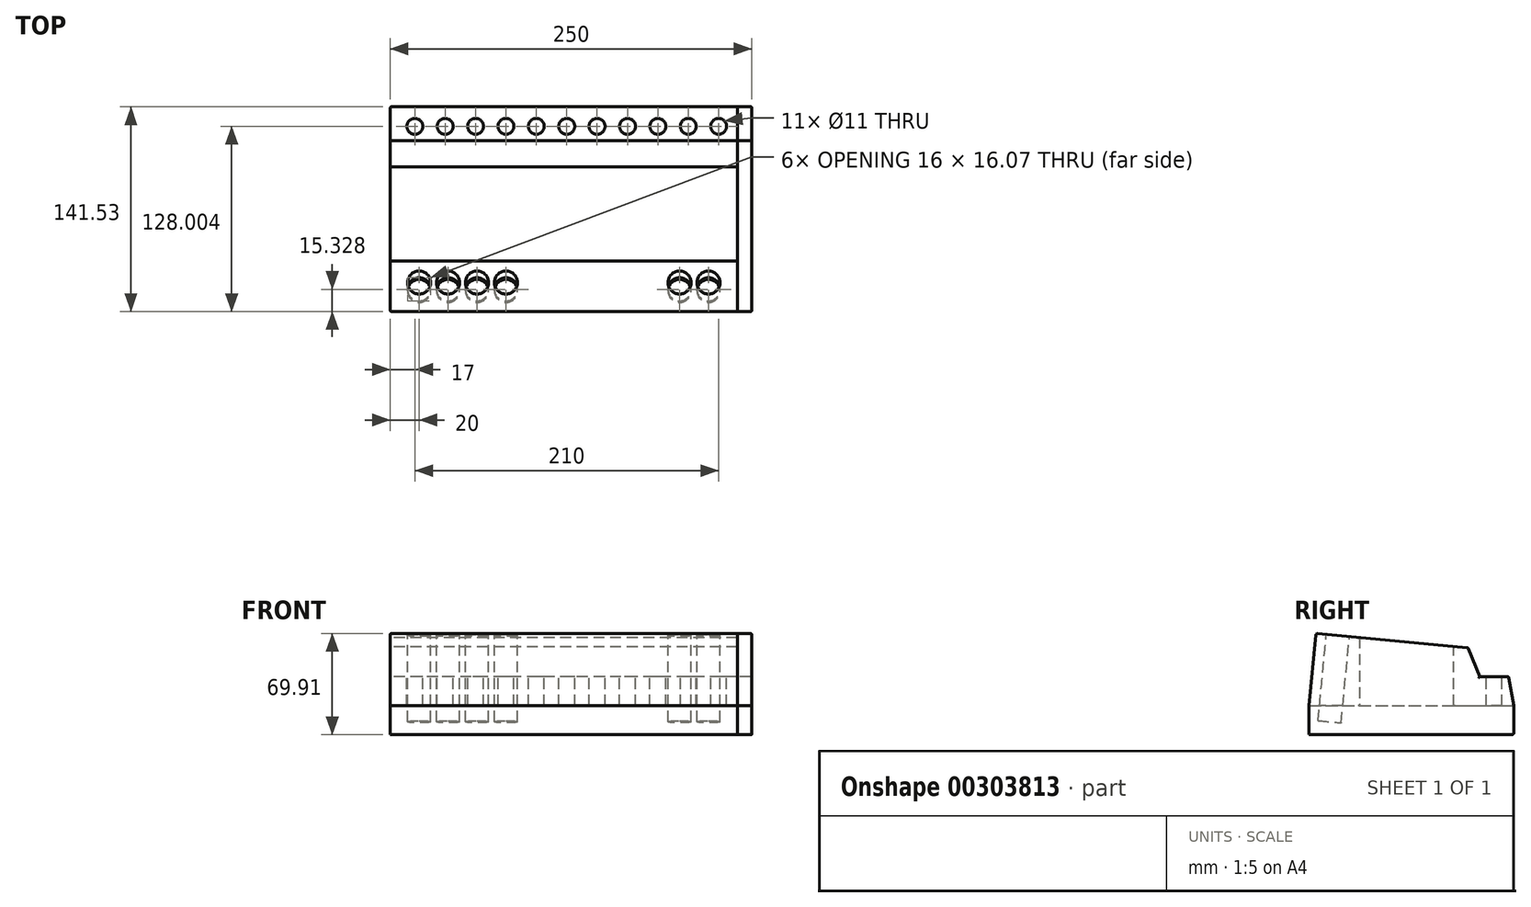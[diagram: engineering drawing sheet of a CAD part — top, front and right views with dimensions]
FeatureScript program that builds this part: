
annotation { "Feature Type Name" : "Feature", "Feature Type Description" : "" }
export const myFeature = defineFeature(function(context is Context, id is Id, definition is map)
    precondition{}
    {
        {
            var Q0;
            Q0=qCreatedBy(makeId("Right.planeOp"),FACE);
            var sketch = newSketch(context, id + "F0", { "sketchPlane" : qUnion([Q0])});
            skLineSegment(sketch, "E0", {"start": v(-106.53, 67.11) * mm, "end": v(-106.53, 20) * mm});
            skLineSegment(sketch, "E1", {"start": v(-41.53, 20) * mm, "end": v(-41.53, 60.85) * mm});
            skLineSegment(sketch, "E2", {"start": v(-41.53, 60.85) * mm, "end": v(-31.57, 59.9) * mm});
            skLineSegment(sketch, "E3", {"start": v(-31.57, 59.9) * mm, "end": v(-23.53, 40) * mm});
            skLineSegment(sketch, "E4", {"start": v(-23.53, 40) * mm, "end": v(-3.53, 40) * mm});
            skLineSegment(sketch, "E5", {"start": v(-3.53, 40) * mm, "end": v(0, 20) * mm});
            skLineSegment(sketch, "E6", {"start": v(-141.53, 20) * mm, "end": v(-136.53, 70) * mm});
            skLineSegment(sketch, "E7", {"start": v(-175.18, 73.72) * mm, "end": v(36.57, 53.33) * mm, "construction": true});
            skLineSegment(sketch, "E8", {"start": v(-136.53, 70) * mm, "end": v(-106.53, 67.11) * mm});
            skLineSegment(sketch, "E9", {"start": v(-141.53, 20) * mm, "end": v(-106.53, 20) * mm});
            skLineSegment(sketch, "E10", {"start": v(-176.43, 20) * mm, "end": v(39.02, 20) * mm, "construction": true});
            skLineSegment(sketch, "E11", {"start": v(-41.53, 20) * mm, "end": v(0, 20) * mm});
            skSolve(sketch);
        }
        {
            var Q0;
            Q0 = qSketchRegion(id + "F0", true);
            extrude(context, id + "F1", {"entities" : qUnion([Q0]), "endBound" : BoundingType.SYMMETRIC, "depth" : 240 * mm});
        }
        {
            var Q0;
            Q0=qCreatedBy(makeId("Right.planeOp"),FACE);
            var sketch = newSketch(context, id + "F2", { "sketchPlane" : qUnion([Q0])});
            skLineSegment(sketch, "E12.bottom", {"start": v(-141.53, 20) * mm, "end": v(0, 20) * mm});
            skLineSegment(sketch, "E12.top", {"start": v(-141.53, 0) * mm, "end": v(0, 0) * mm});
            skLineSegment(sketch, "E12.left", {"start": v(-141.53, 20) * mm, "end": v(-141.53, 0) * mm});
            skLineSegment(sketch, "E12.right", {"start": v(0, 20) * mm, "end": v(0, 0) * mm});
            skSolve(sketch);
        }
        {
            var Q0;
            Q0 = qSketchRegion(id + "F2", true);
            extrude(context, id + "F3", {"entities" : qUnion([Q0]), "endBound" : BoundingType.SYMMETRIC, "depth" : 240 * mm});
        }
        {
            var Q0;
            Q0=makeQuery(id+"F1.opExtrude","SWEPT_FACE",FACE,{"disambiguationData":[OSD([sQuery(id+"F0.wireOp",EDGE,"E8")])]});
            var sketch = newSketch(context, id + "F4", { "sketchPlane" : qUnion([Q0])});
            skLineSegment(sketch, "E13", {"start": v(120, -127.54) * mm, "end": v(-120, -127.54) * mm, "construction": true});
            skCircle(sketch, "E14", {"center": v(-100, -127.54) * mm, "radius": 8 * mm});
            skCircle(sketch, "E15", {"center": v(100, -127.54) * mm, "radius": 8 * mm});
            skCircle(sketch, "E16", {"center": v(80, -127.54) * mm, "radius": 8 * mm});
            skCircle(sketch, "E17.1.0.0", {"center": v(-80, -127.54) * mm, "radius": 8 * mm});
            skCircle(sketch, "E17.2.0.0", {"center": v(-60, -127.54) * mm, "radius": 8 * mm});
            skCircle(sketch, "E17.3.0.0", {"center": v(-40, -127.54) * mm, "radius": 8 * mm});
            skLineSegment(sketch, "E17.direction1", {"start": v(-100, -127.54) * mm, "end": v(-80, -127.54) * mm, "construction": true});
            skSolve(sketch);
        }
        {
            var Q0;
            Q0 = qSketchRegion(id + "F4", true);
            extrude(context, id + "F5", {"entities" : qUnion([Q0]), "operationType" : NewBodyOperationType.REMOVE, "oppositeDirection" : true, "depth" : 60 * mm});
        }
        {
            var Q0;
            Q0=makeQuery(id+"F1.opExtrude","SWEPT_FACE",FACE,{"disambiguationData":[OSD([sQuery(id+"F0.wireOp",EDGE,"E4")])]});
            var sketch = newSketch(context, id + "F6", { "sketchPlane" : qUnion([Q0])});
            skCircle(sketch, "E18", {"center": v(107, -13.53) * mm, "radius": 5.5 * mm});
            skCircle(sketch, "E19.1.0.0", {"center": v(86, -13.53) * mm, "radius": 5.5 * mm});
            skCircle(sketch, "E19.2.0.0", {"center": v(65, -13.53) * mm, "radius": 5.5 * mm});
            skCircle(sketch, "E19.3.0.0", {"center": v(44, -13.53) * mm, "radius": 5.5 * mm});
            skCircle(sketch, "E19.4.0.0", {"center": v(23, -13.53) * mm, "radius": 5.5 * mm});
            skLineSegment(sketch, "E19.direction1", {"start": v(107, -13.53) * mm, "end": v(86, -13.53) * mm, "construction": true});
            skLineSegment(sketch, "E19.direction2", {"start": v(107, -13.53) * mm, "end": v(107, 6.47) * mm, "construction": true});
            skCircle(sketch, "E20.0.5.0", {"center": v(2, -13.53) * mm, "radius": 5.5 * mm});
            skCircle(sketch, "E20.0.6.0", {"center": v(-19, -13.53) * mm, "radius": 5.5 * mm});
            skCircle(sketch, "E20.0.7.0", {"center": v(-40, -13.53) * mm, "radius": 5.5 * mm});
            skCircle(sketch, "E20.0.8.0", {"center": v(-61, -13.53) * mm, "radius": 5.5 * mm});
            skCircle(sketch, "E20.0.9.0", {"center": v(-82, -13.53) * mm, "radius": 5.5 * mm});
            skCircle(sketch, "E21.0.10.0", {"center": v(-103, -13.53) * mm, "radius": 5.5 * mm});
            skSolve(sketch);
        }
        {
            var Q0;
            Q0 = qSketchRegion(id + "F6", true);
            extrude(context, id + "F7", {"entities" : qUnion([Q0]), "operationType" : NewBodyOperationType.REMOVE, "oppositeDirection" : true, "depth" : 20 * mm});
        }
        {
            var Q0;
            Q0=makeQuery(id+"F1.opExtrude","CAP_FACE",FACE,{"disambiguationData":[OSD([sQuery(id+"F0.wireOp",EDGE,"tw387ZvV-JYj8-68VL-s3yb-Uck8thZa5wHs"),sQuery(id+"F0.wireOp",EDGE,"NKL3wcGp-Pg8C-4RBL-oGj4-fkOtX3Kfw7oe"),sQuery(id+"F0.wireOp",EDGE,"E0"),sQuery(id+"F0.wireOp",EDGE,"q42HuZwT-Lavk-Tpkk-W9Jl-RTIdizZQmuwW"),sQuery(id+"F0.wireOp",EDGE,"E1"),sQuery(id+"F0.wireOp",EDGE,"E2"),sQuery(id+"F0.wireOp",EDGE,"E3"),sQuery(id+"F0.wireOp",EDGE,"E4"),sQuery(id+"F0.wireOp",EDGE,"E5"),sQuery(id+"F0.wireOp",EDGE,"b2ctV8Q4-d0uH-XkVO-mPFh-DvxioqJfeffP"),sQuery(id+"F0.wireOp",EDGE,"nbkesUFM-ipBm-tUCA-T4BL-iNUQwh1iUt4A"),sQuery(id+"F0.wireOp",EDGE,"E6")])],"isStart":false});
            var sketch = newSketch(context, id + "F8", { "sketchPlane" : qUnion([Q0])});
            skLineSegment(sketch, "E22", {"start": v(-141.53, 20) * mm, "end": v(-141.53, 20) * mm});
            skLineSegment(sketch, "E23", {"start": v(-141.53, 20) * mm, "end": v(-141.53, 0) * mm});
            skLineSegment(sketch, "E24", {"start": v(-141.53, 0) * mm, "end": v(0, 0) * mm});
            skLineSegment(sketch, "E25", {"start": v(-3.53, 40) * mm, "end": v(-3.53, 40) * mm});
            skLineSegment(sketch, "E26", {"start": v(-3.53, 40) * mm, "end": v(-23.53, 40) * mm});
            skLineSegment(sketch, "E27", {"start": v(-23.53, 40) * mm, "end": v(-31.57, 59.9) * mm});
            skLineSegment(sketch, "E28", {"start": v(-31.57, 59.9) * mm, "end": v(-136.53, 70) * mm});
            skLineSegment(sketch, "E29", {"start": v(-136.53, 70) * mm, "end": v(-141.53, 20) * mm});
            skLineSegment(sketch, "E30", {"start": v(-3.53, 40) * mm, "end": v(0, 20) * mm});
            skLineSegment(sketch, "E31", {"start": v(0, 20) * mm, "end": v(0, 0) * mm});
            skSolve(sketch);
        }
        {
            var Q0;
            Q0 = qSketchRegion(id + "F8", true);
            extrude(context, id + "F9", {"entities" : qUnion([Q0]), "depth" : 10 * mm});
        }
        {
            var Q0;
            Q0=makeQuery(id+"F1.opExtrude","SWEPT_EDGE",EDGE,{"disambiguationData":[OSD([sQuery(id+"F0.wireOp",EDGE,"E4"),sQuery(id+"F0.wireOp",EDGE,"E5")])]});
            var Q1;
            Q1=makeQuery(id+"F1.opExtrude","SWEPT_EDGE",EDGE,{"disambiguationData":[OSD([sQuery(id+"F0.wireOp",EDGE,"E2"),sQuery(id+"F0.wireOp",EDGE,"E3")])]});
            var Q2;
            Q2=makeQuery(id+"F1.opExtrude","SWEPT_EDGE",EDGE,{"disambiguationData":[OSD([sQuery(id+"F0.wireOp",EDGE,"E1"),sQuery(id+"F0.wireOp",EDGE,"E2")])]});
            var Q3;
            Q3=makeQuery(id+"F3.opExtrude","SWEPT_EDGE",EDGE,{"disambiguationData":[OSD([sQuery(id+"F2.wireOp",EDGE,"E12.top"),sQuery(id+"F2.wireOp",EDGE,"E12.right")])]});
            var Q4;
            Q4=makeQuery(id+"F9.opExtrude","SWEPT_EDGE",EDGE,{"disambiguationData":[OSD([sQuery(id+"F8.wireOp",EDGE,"E24"),sQuery(id+"F8.wireOp",EDGE,"E31")])]});
            var Q5;
            Q5=makeQuery(id+"F9.opExtrude","SWEPT_EDGE",EDGE,{"disambiguationData":[OSD([sQuery(id+"F8.wireOp",EDGE,"E26"),sQuery(id+"F8.wireOp",EDGE,"E30")])]});
            var Q6;
            Q6=makeQuery(id+"F9.opExtrude","SWEPT_EDGE",EDGE,{"disambiguationData":[OSD([sQuery(id+"F8.wireOp",EDGE,"E27"),sQuery(id+"F8.wireOp",EDGE,"E28")])]});
            var Q7;
            Q7=makeQuery(id+"F3.opExtrude","CAP_EDGE",EDGE,{"disambiguationData":[OSD([sQuery(id+"F2.wireOp",EDGE,"E12.right")])],"isStart":true});
            var Q8;
            Q8=makeQuery(id+"F1.opExtrude","CAP_EDGE",EDGE,{"disambiguationData":[OSD([sQuery(id+"F0.wireOp",EDGE,"E5")])],"isStart":true});
            var Q9;
            Q9=makeQuery(id+"F1.opExtrude","CAP_EDGE",EDGE,{"disambiguationData":[OSD([sQuery(id+"F0.wireOp",EDGE,"E4")])],"isStart":true});
            var Q10;
            Q10=makeQuery(id+"F1.opExtrude","CAP_EDGE",EDGE,{"disambiguationData":[OSD([sQuery(id+"F0.wireOp",EDGE,"E3")])],"isStart":true});
            var Q11;
            Q11=makeQuery(id+"F1.opExtrude","CAP_EDGE",EDGE,{"disambiguationData":[OSD([sQuery(id+"F0.wireOp",EDGE,"E2")])],"isStart":true});
            var Q12;
            Q12=makeQuery(id+"F1.opExtrude","CAP_EDGE",EDGE,{"disambiguationData":[OSD([sQuery(id+"F0.wireOp",EDGE,"E1")])],"isStart":true});
            var Q13;
            Q13=makeQuery(id+"F1.opExtrude","CAP_EDGE",EDGE,{"disambiguationData":[OSD([sQuery(id+"F0.wireOp",EDGE,"E0")])],"isStart":true});
            var Q14;
            Q14=makeQuery(id+"F1.opExtrude","CAP_EDGE",EDGE,{"disambiguationData":[OSD([sQuery(id+"F0.wireOp",EDGE,"E8")])],"isStart":true});
            var Q15;
            Q15=makeQuery(id+"F1.opExtrude","CAP_EDGE",EDGE,{"disambiguationData":[OSD([sQuery(id+"F0.wireOp",EDGE,"E6")])],"isStart":true});
            var Q16;
            Q16=makeQuery(id+"F3.opExtrude","CAP_EDGE",EDGE,{"disambiguationData":[OSD([sQuery(id+"F2.wireOp",EDGE,"E12.left")])],"isStart":true});
            var Q17;
            Q17=makeQuery(id+"F1.opExtrude","SWEPT_EDGE",EDGE,{"disambiguationData":[OSD([sQuery(id+"F0.wireOp",EDGE,"E6"),sQuery(id+"F0.wireOp",EDGE,"E8")])]});
            var Q18;
            Q18=makeQuery(id+"F9.opExtrude","SWEPT_EDGE",EDGE,{"disambiguationData":[OSD([sQuery(id+"F8.wireOp",EDGE,"E28"),sQuery(id+"F8.wireOp",EDGE,"E29")])]});
            var Q19;
            Q19=makeQuery(id+"F9.opExtrude","CAP_EDGE",EDGE,{"disambiguationData":[OSD([sQuery(id+"F8.wireOp",EDGE,"E29")])],"isStart":false});
            var Q20;
            Q20=makeQuery(id+"F9.opExtrude","CAP_EDGE",EDGE,{"disambiguationData":[OSD([sQuery(id+"F8.wireOp",EDGE,"E23")])],"isStart":false});
            var Q21;
            Q21=makeQuery(id+"F9.opExtrude","CAP_EDGE",EDGE,{"disambiguationData":[OSD([sQuery(id+"F8.wireOp",EDGE,"E28")])],"isStart":false});
            var Q22;
            Q22=makeQuery(id+"F9.opExtrude","CAP_EDGE",EDGE,{"disambiguationData":[OSD([sQuery(id+"F8.wireOp",EDGE,"E27")])],"isStart":false});
            var Q23;
            Q23=makeQuery(id+"F9.opExtrude","CAP_EDGE",EDGE,{"disambiguationData":[OSD([sQuery(id+"F8.wireOp",EDGE,"E26")])],"isStart":false});
            var Q24;
            Q24=makeQuery(id+"F9.opExtrude","CAP_EDGE",EDGE,{"disambiguationData":[OSD([sQuery(id+"F8.wireOp",EDGE,"E30")])],"isStart":false});
            var Q25;
            Q25=makeQuery(id+"F9.opExtrude","CAP_EDGE",EDGE,{"disambiguationData":[OSD([sQuery(id+"F8.wireOp",EDGE,"E31")])],"isStart":false});
            fillet(context, id + "F10", {"entities" : qUnion([Q0, Q1, Q2, Q3, Q4, Q5, Q6, Q7, Q8, Q9, Q10, Q11, Q12, Q13, Q14, Q15, Q16, Q17, Q18, Q19, Q20, Q21, Q22, Q23, Q24, Q25]), "radius" : 1 * mm, "tangentPropagation" : true, "allowEdgeOverflow" : false});
        }
    });
